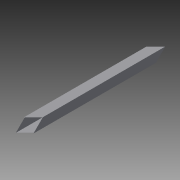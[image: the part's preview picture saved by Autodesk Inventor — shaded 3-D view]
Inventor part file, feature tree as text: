
AUTODESK INVENTOR PART (.ipt)
format: ipt  version: 2015 (Build 190159000, 159)  size: 90,112 bytes
history: native  units: in
note: dims shown in document units (in); Inventor stores cm internally (conversion verified against a paired STEP export)
features: extrude x2, sketch x2
ambient origin geometry x8: Origin, YZ Plane, XZ Plane, XY Plane, X Axis, Y Axis, Z Axis, Center Point
bodies: Solid1 (feature_tree)
feature tree (4):
  extrude  "Extrusion1"  Depth=2.0in
  extrude  "Extrusion2"  Depth=0.083in TaperAngle=0.0deg
  sketch  "Sketch1"  dims[d0=2.0in d1=2.0in]
  sketch  "Sketch2"  dims[d2=0.083in d3=33.0in d4=0.0in d7=1.0994in d9=30.0in d10=0.0in d11=1.0994in]
